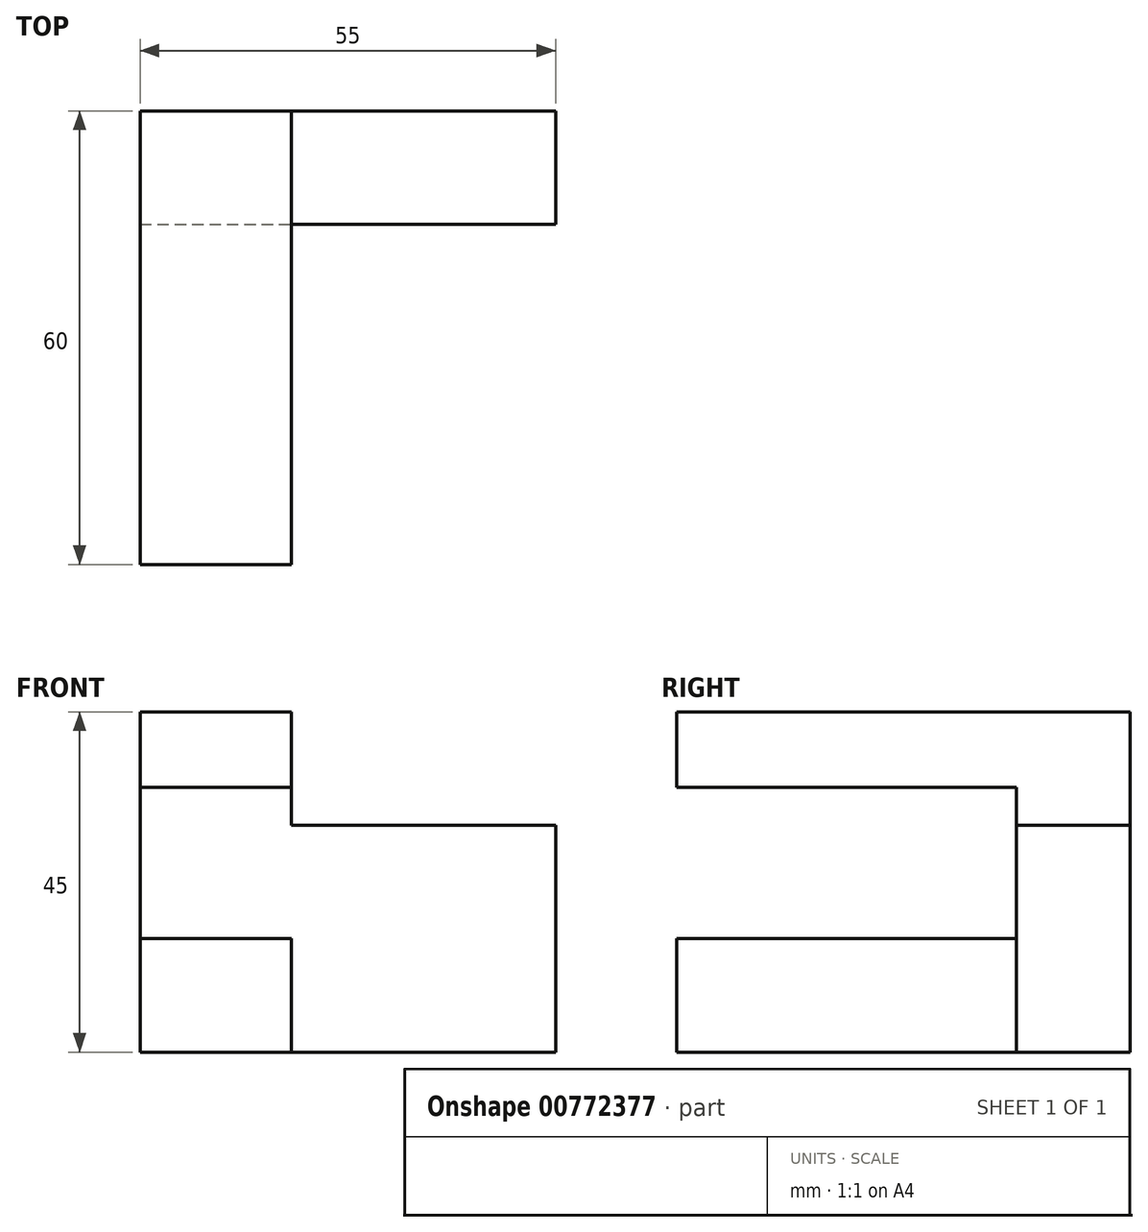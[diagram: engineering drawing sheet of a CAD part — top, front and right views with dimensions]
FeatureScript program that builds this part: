
annotation { "Feature Type Name" : "Feature", "Feature Type Description" : "" }
export const myFeature = defineFeature(function(context is Context, id is Id, definition is map)
    precondition{}
    {
        {
            var Q0;
            Q0=qCreatedBy(makeId("Right.planeOp"),FACE);
            var sketch = newSketch(context, id + "F0", { "sketchPlane" : qUnion([Q0])});
            skLineSegment(sketch, "E0", {"start": v(0, 0) * mm, "end": v(0, 15) * mm});
            skLineSegment(sketch, "E1", {"start": v(0, 15) * mm, "end": v(45, 15) * mm});
            skLineSegment(sketch, "E2", {"start": v(45, 15) * mm, "end": v(45, 35) * mm});
            skLineSegment(sketch, "E3", {"start": v(45, 35) * mm, "end": v(0, 35) * mm});
            skLineSegment(sketch, "E4", {"start": v(0, 35) * mm, "end": v(0, 45) * mm});
            skLineSegment(sketch, "E5", {"start": v(0, 45) * mm, "end": v(60, 45) * mm});
            skLineSegment(sketch, "E6", {"start": v(60, 45) * mm, "end": v(60, 0) * mm});
            skLineSegment(sketch, "E7", {"start": v(60, 0) * mm, "end": v(0, 0) * mm});
            skLineSegment(sketch, "E8", {"start": v(45, 30) * mm, "end": v(60, 30) * mm});
            skLineSegment(sketch, "E9", {"start": v(45, 15) * mm, "end": v(45, 0) * mm});
            skSolve(sketch);
        }
        {
            var Q0;
            {var subQ1=sQuery(id+"F0.wireOp",EDGE,"E3");Q0=makeQuery(id+"F0.imprint","IMPRINT",FACE,{"disambiguationData":[TD([[makeQuery(id+"F0.imprint","IMPRINT",EDGE,{"derivedFrom":subQ1}),-1.0]])]});}
            var Q1;
            {var subQ0=sQuery(id+"F0.wireOp",EDGE,"E8");Q1=makeQuery(id+"F0.imprint","IMPRINT",FACE,{"disambiguationData":[TD([[makeQuery(id+"F0.imprint","IMPRINT",EDGE,{"derivedFrom":subQ0}),-1.0]])]});}
            var Q2;
            {var subQ0=sQuery(id+"F0.wireOp",EDGE,"E0");Q2=makeQuery(id+"F0.imprint","IMPRINT",FACE,{"disambiguationData":[TD([[makeQuery(id+"F0.imprint","IMPRINT",EDGE,{"derivedFrom":subQ0}),-1.0]])]});}
            extrude(context, id + "F1", {"entities" : qUnion([Q0, Q1, Q2]), "oppositeDirection" : true, "depth" : 20 * mm, "offsetDistance" : 25 * mm});
        }
        {
            var Q0;
            {var subQ0=sQuery(id+"F0.wireOp",EDGE,"E8");Q0=makeQuery(id+"F0.imprint","IMPRINT",FACE,{"disambiguationData":[TD([[makeQuery(id+"F0.imprint","IMPRINT",EDGE,{"derivedFrom":subQ0}),-1.0]])]});}
            extrude(context, id + "F2", {"entities" : qUnion([Q0]), "operationType" : NewBodyOperationType.ADD, "depth" : 35 * mm, "offsetDistance" : 25 * mm});
        }
    });
